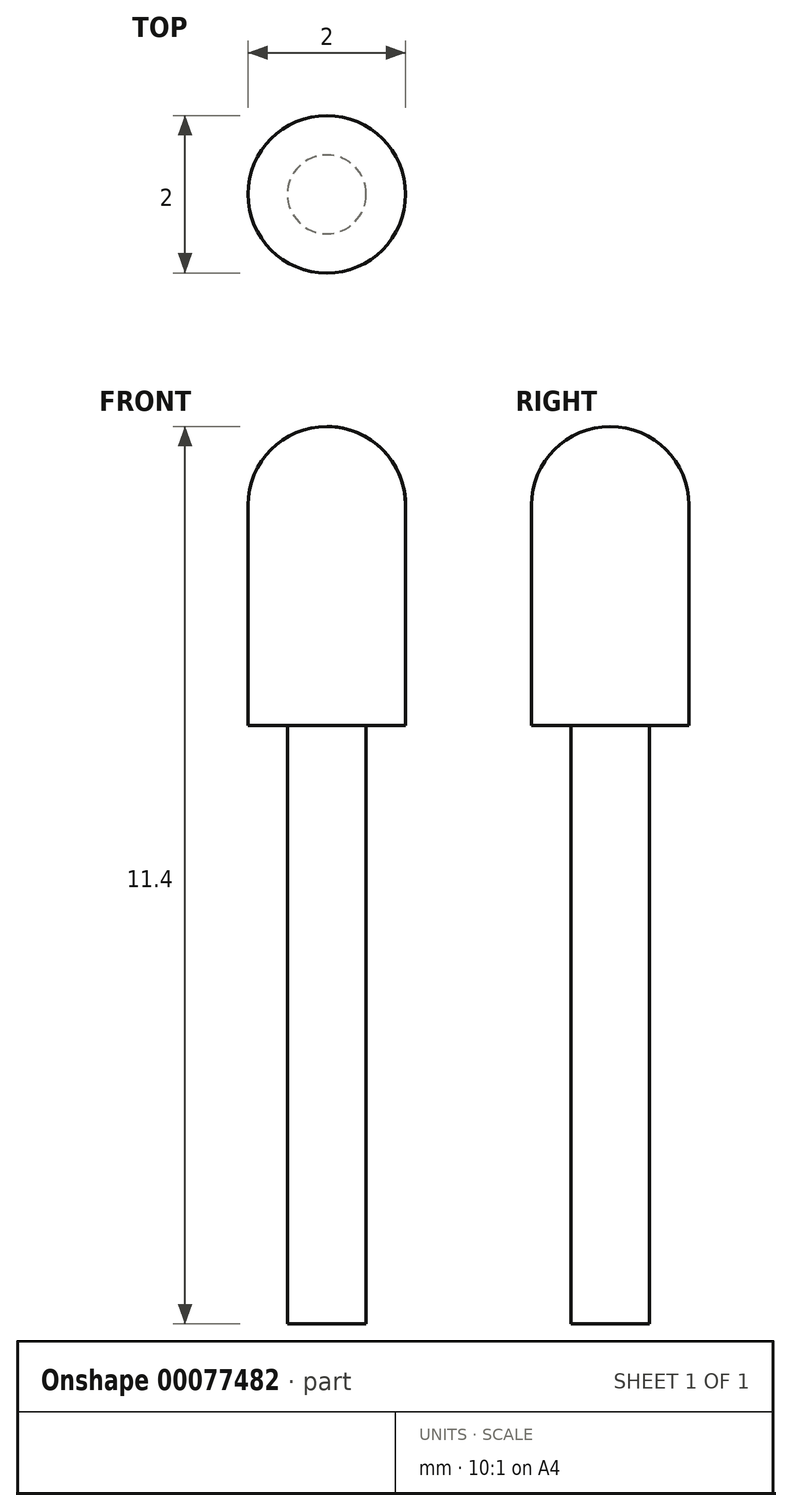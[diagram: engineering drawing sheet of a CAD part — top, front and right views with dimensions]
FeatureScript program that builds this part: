
annotation { "Feature Type Name" : "Feature", "Feature Type Description" : "" }
export const myFeature = defineFeature(function(context is Context, id is Id, definition is map)
    precondition{}
    {
        {
            var Q0;
            Q0=qCreatedBy(makeId("Top.planeOp"),FACE);
            var sketch = newSketch(context, id + "F0", { "sketchPlane" : qUnion([Q0])});
            skCircle(sketch, "E0", {"center": v(0, 0) * mm, "radius": 0.5 * mm});
            skSolve(sketch);
        }
        {
            var Q0;
            Q0=makeQuery(id+"F0.imprint","IMPRINT",FACE,{"disambiguationData":[TD([[makeQuery(id+"F0.imprint","IMPRINT",EDGE,{"derivedFrom":sQuery(id+"F0.wireOp",EDGE,"E0")}),1.0]])]});
            extrude(context, id + "F1", {"entities" : qUnion([Q0]), "depth" : 7.6 * mm});
        }
        {
            var Q0;
            Q0=makeQuery(id+"F1.opExtrude","CAP_FACE",FACE,{"disambiguationData":[OSD([sQuery(id+"F0.wireOp",EDGE,"E0")])],"isStart":false});
            var sketch = newSketch(context, id + "F2", { "sketchPlane" : qUnion([Q0])});
            skCircle(sketch, "E1", {"center": v(0, 0) * mm, "radius": 1 * mm});
            skSolve(sketch);
        }
        {
            var Q0;
            {var subQ0=makeQuery(id+"F2.imprint","IMPRINT",EDGE,{"derivedFrom":makeQuery(id+"F1.opExtrude","CAP_EDGE",EDGE,{"disambiguationData":[OSD([sQuery(id+"F0.wireOp",EDGE,"E0")])],"isStart":false})});Q0=qUnion([makeQuery(id+"F2.imprint","IMPRINT",FACE,{"disambiguationData":[TD([[makeQuery(id+"F2.imprint","IMPRINT",EDGE,{"derivedFrom":sQuery(id+"F2.wireOp",EDGE,"E1")}),1.0]])]}),makeQuery(id+"F2.imprint","IMPRINT",FACE,{"disambiguationData":[TD([[subQ0,1.0]])]})]);}
            extrude(context, id + "F3", {"entities" : qUnion([Q0]), "operationType" : NewBodyOperationType.ADD, "depth" : 2.8 * mm});
        }
        {
            var Q0;
            Q0=qCreatedBy(makeId("Front.planeOp"),FACE);
            var sketch = newSketch(context, id + "F4", { "sketchPlane" : qUnion([Q0])});
            skLineSegment(sketch, "E2", {"start": v(0, 0) * mm, "end": v(0, 15) * mm, "construction": true});
            skArc(sketch, "E3", {"start": v(1, 10.4) * mm, "mid": v(0.7, 11.1) * mm, "end": v(0, 11.4) * mm});
            skLineSegment(sketch, "E4", {"start": v(0, 10.4) * mm, "end": v(0, 11.4) * mm});
            skLineSegment(sketch, "E5", {"start": v(0, 10.4) * mm, "end": v(1, 10.4) * mm});
            skSolve(sketch);
        }
        {
            var Q0;
            Q0=makeQuery(id+"F4.imprint","IMPRINT",FACE,{"disambiguationData":[TD([[makeQuery(id+"F4.imprint","IMPRINT",EDGE,{"derivedFrom":sQuery(id+"F4.wireOp",EDGE,"E3")}),1.0]])]});
            var Q1;
            Q1=sQuery(id+"F4.wireOp",EDGE,"E2");
            revolve(context, id + "F5", {"operationType" : NewBodyOperationType.ADD, "entities" : qUnion([Q0]), "axis" : qUnion([Q1]), "revolveType" : RevolveType.FULL});
        }
    });
